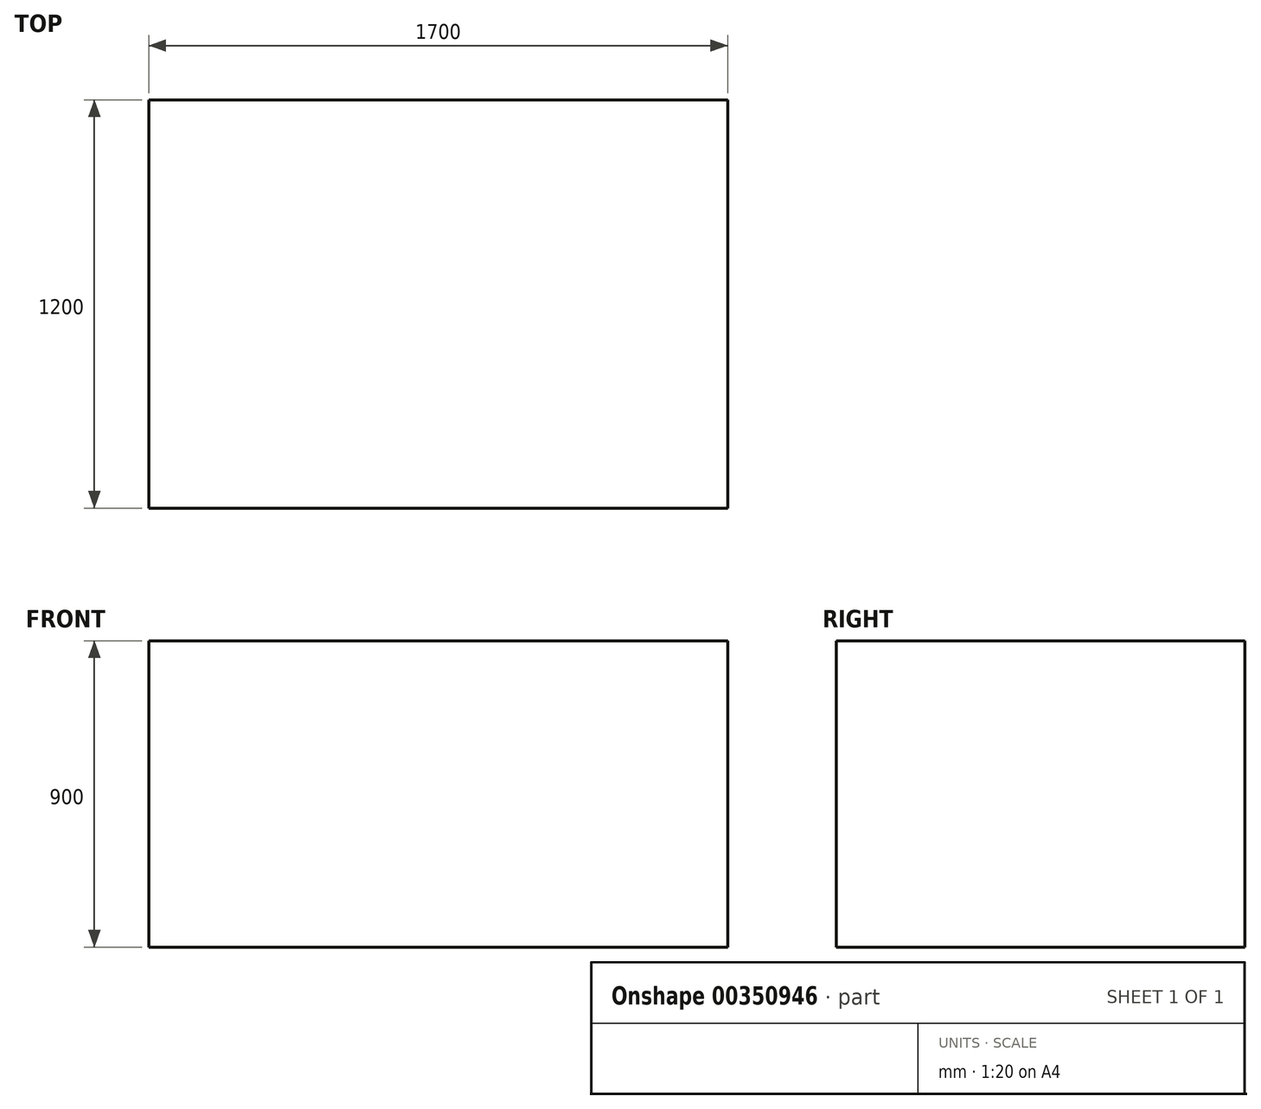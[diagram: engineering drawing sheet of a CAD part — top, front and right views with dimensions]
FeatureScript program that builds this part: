
annotation { "Feature Type Name" : "Feature", "Feature Type Description" : "" }
export const myFeature = defineFeature(function(context is Context, id is Id, definition is map)
    precondition{}
    {
        {
            var Q0;
            Q0=qCreatedBy(makeId("Front.planeOp"),FACE);
            var sketch = newSketch(context, id + "F0", { "sketchPlane" : qUnion([Q0])});
            skLineSegment(sketch, "E0.bottom", {"start": v(-850, 450) * mm, "end": v(850, 450) * mm});
            skLineSegment(sketch, "E0.top", {"start": v(-850, -450) * mm, "end": v(850, -450) * mm});
            skLineSegment(sketch, "E0.left", {"start": v(-850, 450) * mm, "end": v(-850, -450) * mm});
            skLineSegment(sketch, "E0.right", {"start": v(850, 450) * mm, "end": v(850, -450) * mm});
            skPoint(sketch, "E0.middle", {"position": v(0, 0) * mm});
            skSolve(sketch);
        }
        {
            var Q0;
            Q0 = qSketchRegion(id + "F0", true);
            extrude(context, id + "F1", {"entities" : qUnion([Q0]), "depth" : 1200 * mm});
        }
    });
